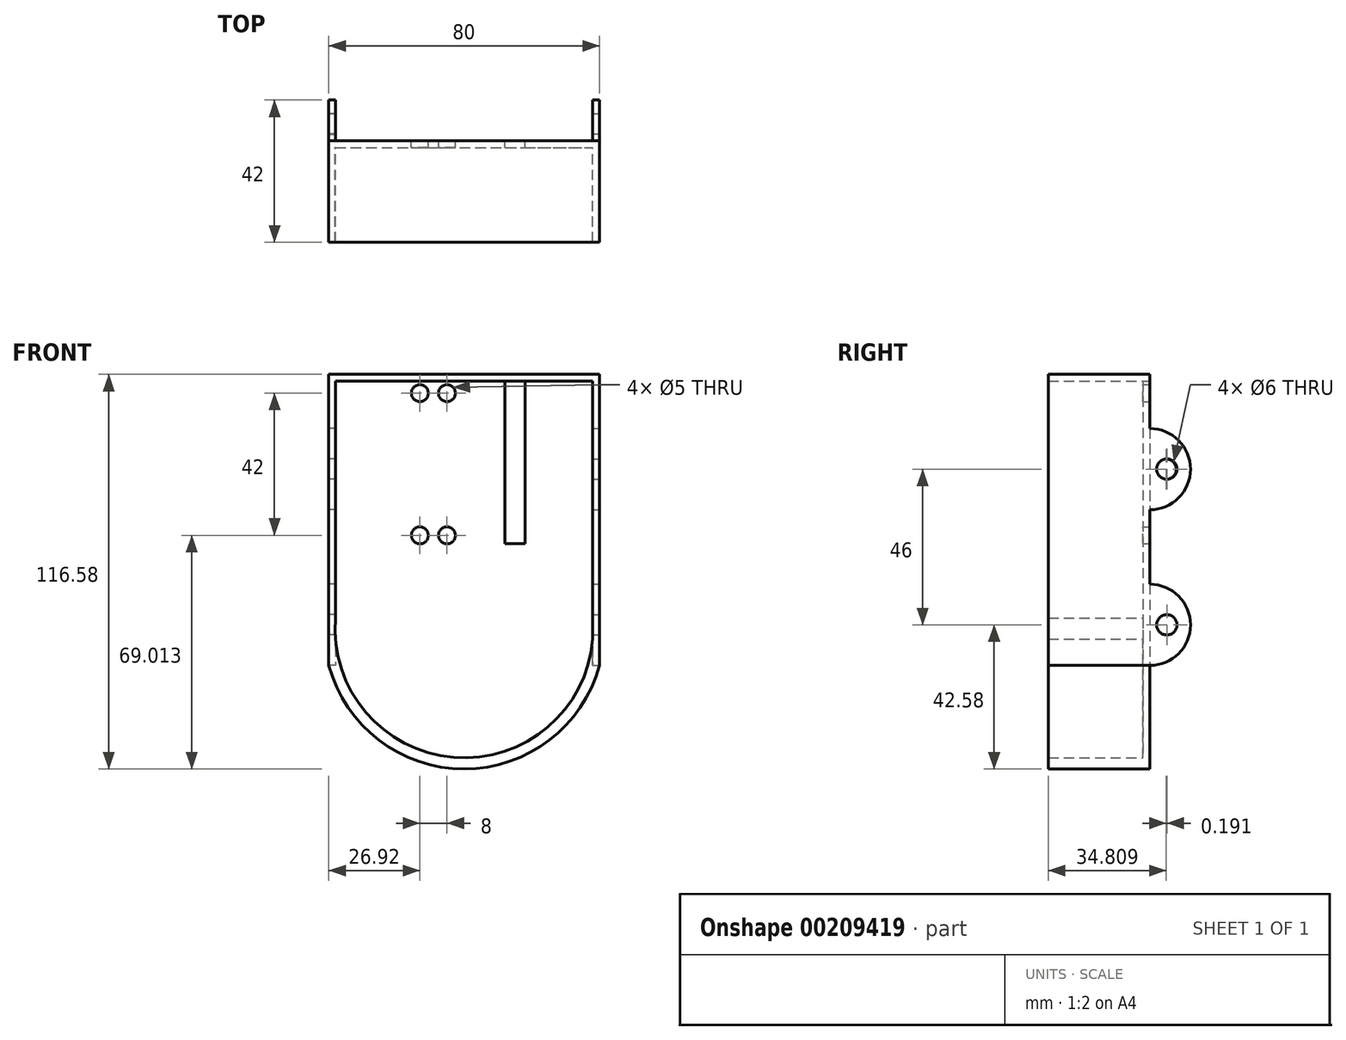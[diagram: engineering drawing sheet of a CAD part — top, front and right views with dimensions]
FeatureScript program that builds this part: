
annotation { "Feature Type Name" : "Feature", "Feature Type Description" : "" }
export const myFeature = defineFeature(function(context is Context, id is Id, definition is map)
    precondition{}
    {
        {
            var Q0;
            Q0=qCreatedBy(makeId("Front.planeOp"),FACE);
            var sketch = newSketch(context, id + "F0", { "sketchPlane" : qUnion([Q0])});
            skLineSegment(sketch, "E0.bottom", {"start": v(40, 43) * mm, "end": v(-40, 43) * mm});
            skLineSegment(sketch, "E0.left", {"start": v(40, 43) * mm, "end": v(40, -43) * mm});
            skLineSegment(sketch, "E0.right", {"start": v(-40, 43) * mm, "end": v(-40, -43) * mm});
            skLineSegment(sketch, "E1", {"start": v(-40, -43) * mm, "end": v(-40, -65.96) * mm, "construction": true});
            skLineSegment(sketch, "E2", {"start": v(-40, -43) * mm, "end": v(-22.67, -60.33) * mm, "construction": true});
            skArc(sketch, "E3", {"start": v(-40, -43) * mm, "mid": v(0, -73.58) * mm, "end": v(40, -43) * mm});
            skLineSegment(sketch, "E4.bottom", {"start": v(-38, 41) * mm, "end": v(38, 41) * mm});
            skLineSegment(sketch, "E4.left", {"start": v(-38, 41) * mm, "end": v(-38, -29) * mm});
            skLineSegment(sketch, "E4.right", {"start": v(38, 41) * mm, "end": v(38, -35.25) * mm});
            skLineSegment(sketch, "E5", {"start": v(-38, -29) * mm, "end": v(-38, -51.9) * mm, "construction": true});
            skLineSegment(sketch, "E6", {"start": v(-38, -29) * mm, "end": v(-22.92, -44.08) * mm, "construction": true});
            skArc(sketch, "E7", {"start": v(-38, -29) * mm, "mid": v(-3.13, -70.13) * mm, "end": v(38, -35.25) * mm});
            skLineSegment(sketch, "E8.bottom", {"start": v(12, 41) * mm, "end": v(18, 41) * mm});
            skLineSegment(sketch, "E8.top", {"start": v(12, -7) * mm, "end": v(18, -7) * mm});
            skLineSegment(sketch, "E8.left", {"start": v(12, 41) * mm, "end": v(12, -7) * mm});
            skLineSegment(sketch, "E8.right", {"start": v(18, 41) * mm, "end": v(18, -7) * mm});
            skCircle(sketch, "E9", {"center": v(-13.08, 37.43) * mm, "radius": 2.5 * mm});
            skCircle(sketch, "E10.0.1.0", {"center": v(-13.08, -4.57) * mm, "radius": 2.5 * mm});
            skCircle(sketch, "E10.1.0.0", {"center": v(-5.08, 37.43) * mm, "radius": 2.5 * mm});
            skCircle(sketch, "E10.1.1.0", {"center": v(-5.08, -4.57) * mm, "radius": 2.5 * mm});
            skLineSegment(sketch, "E10.direction1", {"start": v(-13.08, 37.43) * mm, "end": v(-5.08, 37.43) * mm, "construction": true});
            skLineSegment(sketch, "E10.direction2", {"start": v(-13.08, 37.43) * mm, "end": v(-13.08, -4.57) * mm, "construction": true});
            skSolve(sketch);
        }
        {
            var Q0;
            Q0=makeQuery(id+"F0.imprint","IMPRINT",FACE,{"disambiguationData":[TD([[makeQuery(id+"F0.imprint","IMPRINT",EDGE,{"derivedFrom":sQuery(id+"F0.wireOp",EDGE,"E0.bottom")}),1.0]])]});
            extrude(context, id + "F1", {"entities" : qUnion([Q0]), "depth" : 30 * mm});
        }
        {
            var Q0;
            Q0=makeQuery(id+"F0.imprint","IMPRINT",FACE,{"disambiguationData":[TD([[makeQuery(id+"F0.imprint","IMPRINT",EDGE,{"derivedFrom":sQuery(id+"F0.wireOp",EDGE,"E4.bottom")}),-1.0]])]});
            extrude(context, id + "F2", {"entities" : qUnion([Q0]), "operationType" : NewBodyOperationType.ADD, "depth" : 2 * mm});
        }
        {
            var Q0;
            Q0=makeQuery(id+"F1.opExtrude","SWEPT_FACE",FACE,{"disambiguationData":[OSD([sQuery(id+"F0.wireOp",EDGE,"E0.left")])]});
            var sketch = newSketch(context, id + "F3", { "sketchPlane" : qUnion([Q0])});
            skLineSegment(sketch, "E11.0.0", {"start": v(0, -43) * mm, "end": v(0, 43) * mm});
            skLineSegment(sketch, "E11.0.1", {"start": v(0, 43) * mm, "end": v(-30, 43) * mm});
            skLineSegment(sketch, "E11.0.2", {"start": v(-30, 43) * mm, "end": v(-30, -43) * mm});
            skLineSegment(sketch, "E11.0.3", {"start": v(-30, -43) * mm, "end": v(0, -43) * mm});
            skArc(sketch, "E12", {"start": v(0, 3) * mm, "mid": v(12, 15) * mm, "end": v(0, 27) * mm});
            skArc(sketch, "E13", {"start": v(0, -43) * mm, "mid": v(12, -31) * mm, "end": v(0, -19) * mm});
            skCircle(sketch, "E14", {"center": v(5, 15) * mm, "radius": 3 * mm});
            skCircle(sketch, "E15", {"center": v(5, -31) * mm, "radius": 3 * mm});
            skLineSegment(sketch, "E16", {"start": v(0, 15) * mm, "end": v(5, 15) * mm, "construction": true});
            skLineSegment(sketch, "E17", {"start": v(0, -31) * mm, "end": v(5, -31) * mm, "construction": true});
            skSolve(sketch);
        }
        {
            var Q0;
            {var subQ0=sQuery(id+"F3.wireOp",EDGE,"E12");Q0=makeQuery(id+"F3.imprint","IMPRINT",FACE,{"disambiguationData":[TD([[makeQuery(id+"F3.imprint","IMPRINT",EDGE,{"derivedFrom":subQ0}),1.0]])]});}
            var Q1;
            {var subQ0=sQuery(id+"F3.wireOp",EDGE,"E13");Q1=makeQuery(id+"F3.imprint","IMPRINT",FACE,{"disambiguationData":[TD([[makeQuery(id+"F3.imprint","IMPRINT",EDGE,{"derivedFrom":subQ0}),1.0]])]});}
            extrude(context, id + "F4", {"entities" : qUnion([Q0, Q1]), "operationType" : NewBodyOperationType.ADD, "oppositeDirection" : true, "depth" : 2 * mm});
        }
        {
            var Q0;
            Q0=makeQuery(id+"F1.opExtrude","SWEPT_FACE",FACE,{"disambiguationData":[OSD([sQuery(id+"F0.wireOp",EDGE,"E0.right")])]});
            var sketch = newSketch(context, id + "F5", { "sketchPlane" : qUnion([Q0])});
            skLineSegment(sketch, "E18.0.0", {"start": v(0, 43) * mm, "end": v(0, -43) * mm});
            skLineSegment(sketch, "E18.0.1", {"start": v(0, -43) * mm, "end": v(30, -43) * mm});
            skLineSegment(sketch, "E18.0.2", {"start": v(30, -43) * mm, "end": v(30, 43) * mm});
            skLineSegment(sketch, "E18.0.3", {"start": v(30, 43) * mm, "end": v(0, 43) * mm});
            skArc(sketch, "E19", {"start": v(0, 27) * mm, "mid": v(-12, 15) * mm, "end": v(0, 3) * mm});
            skArc(sketch, "E20", {"start": v(0, -19) * mm, "mid": v(-12, -31) * mm, "end": v(0, -43) * mm});
            skCircle(sketch, "E21", {"center": v(-5, -31) * mm, "radius": 3 * mm});
            skCircle(sketch, "E22", {"center": v(-4.8, 14.98) * mm, "radius": 3 * mm});
            skLineSegment(sketch, "E23", {"start": v(0, -31) * mm, "end": v(-5, -31) * mm, "construction": true});
            skSolve(sketch);
        }
        {
            var Q0;
            {var subQ0=sQuery(id+"F5.wireOp",EDGE,"E20");Q0=makeQuery(id+"F5.imprint","IMPRINT",FACE,{"disambiguationData":[TD([[makeQuery(id+"F5.imprint","IMPRINT",EDGE,{"derivedFrom":subQ0}),1.0]])]});}
            var Q1;
            {var subQ0=sQuery(id+"F5.wireOp",EDGE,"E19");Q1=makeQuery(id+"F5.imprint","IMPRINT",FACE,{"disambiguationData":[TD([[makeQuery(id+"F5.imprint","IMPRINT",EDGE,{"derivedFrom":subQ0}),1.0]])]});}
            extrude(context, id + "F6", {"entities" : qUnion([Q0, Q1]), "operationType" : NewBodyOperationType.ADD, "oppositeDirection" : true, "depth" : 2 * mm});
        }
    });
